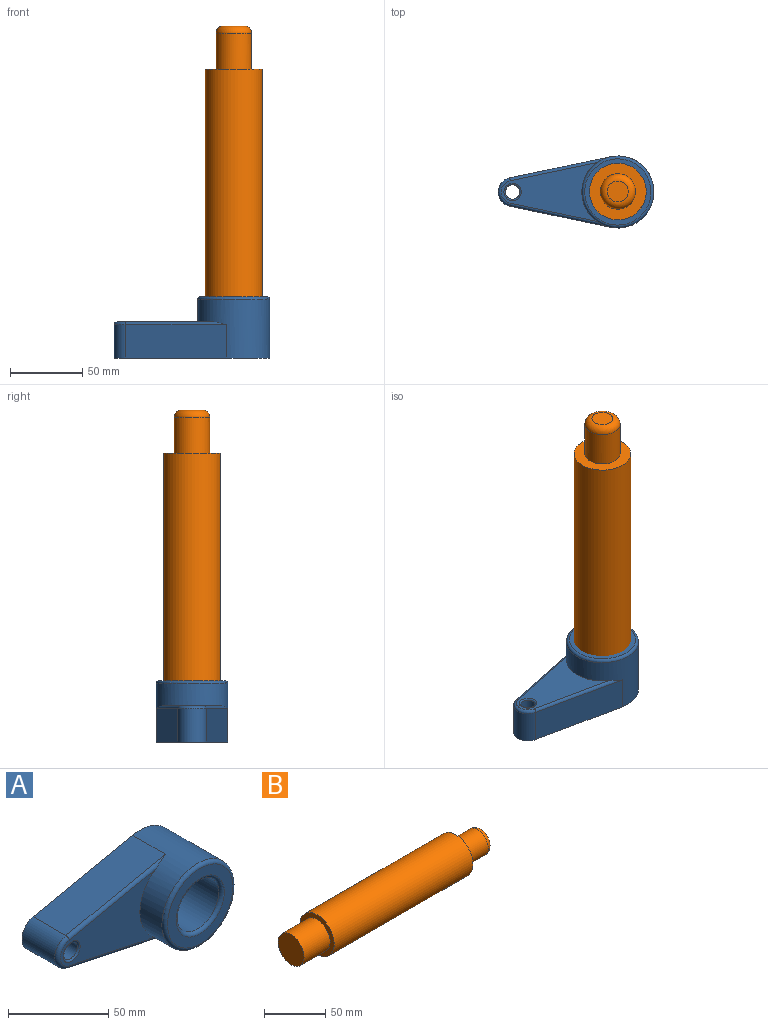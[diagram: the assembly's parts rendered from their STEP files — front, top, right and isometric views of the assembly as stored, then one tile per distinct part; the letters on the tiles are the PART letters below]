
ASSEMBLY  parts=2 mates=1
PART A: 15 faces, bbox 111x42.5x54.1 mm
  f0: plane 66.77x41mm, normal (0,-1,0), area 1365.2mm2, adj f5,f11,f12,f13,f14
  f1: plane 70x23mm, normal (-0.21,0,0.98), area 1645mm2, adj f2,f5,f7,f11
  f2: cylinder r=10mm len=23mm, axis (0,1,0), area 627.5mm2, adj f1,f3,f7,f12
  f3: plane 70x23mm, normal (-0.21,0,-0.98), area 1645mm2, adj f2,f5,f7,f13
  f4: cylinder r=15mm len=40.5mm, axis (0,1,0), area 3817mm2, adj f7,f9
  f5: cylinder r=25mm len=50mm, axis (0,1,0), area 4672.3mm2, adj f0,f1,f3,f7,f10,f11,f13
  f6: cylinder r=5mm len=24mm, axis (0,1,0), area 754mm2, adj f7,f14
  f7: plane 108.08x50mm, normal (0,1,0), area 2965.3mm2, adj f1,f2,f3,f4,f5,f6
  f8: plane 46x46mm, normal (0,-1,0), area 754mm2, adj f9,f10
  f9: torus R=17mm, axis (0,-1,0), area 310.4mm2, adj f4,f8
  f10: torus R=23mm, axis (0,-1,0), area 479.1mm2, adj f5,f8
  f11: cylinder r=2mm len=70.41mm, axis (0.98,0,0.21), area 208.3mm2, adj f0,f1,f5,f12
  f12: torus R=8mm, axis (0,-1,0), area 79.5mm2, adj f0,f2,f11,f13
  f13: cylinder r=2mm len=70.41mm, axis (-0.98,0,0.21), area 208.3mm2, adj f0,f3,f5,f12
  f14: torus R=6mm, axis (0,-1,0), area 52.9mm2, adj f0,f6
PART B: 8 faces, bbox 220x39.4x39.4 mm
  f0: cylinder r=19.7mm len=160mm, axis (-1,0,0), area 19808.8mm2, adj f1,f6
  f1: plane 39.41x39.41mm, normal (-1,0,0), area 512.9mm2, adj f0,f2
  f2: cylinder r=15mm len=30mm, axis (-1,0,0), area 2827.4mm2, adj f1,f3
  f3: plane 30x30mm, normal (-1,0,0), area 706.9mm2, adj f2
  f4: plane 14.5x14.5mm, normal (1,0,0), area 165.1mm2, adj f7
  f5: cylinder r=12.25mm len=25mm, axis (-1,0,0), area 1924mm2, adj f6,f7
  f6: plane 39.41x39.41mm, normal (1,0,0), area 748.4mm2, adj f0,f5
  f7: torus R=7.25mm, axis (1,0,0), area 514.8mm2, adj f4,f5
PLACE A rot(axis=(-1,0,0),90deg) t=(-12.79,-30.72,15.23)mm
PLACE B rot(axis=(0,-1,0),90deg) t=(2.27,-23.23,84.76)mm
MATE fastened B.f0 <-> A.f4  axis (0,0,-1) through (2.27,-23.23,43.23)mm
